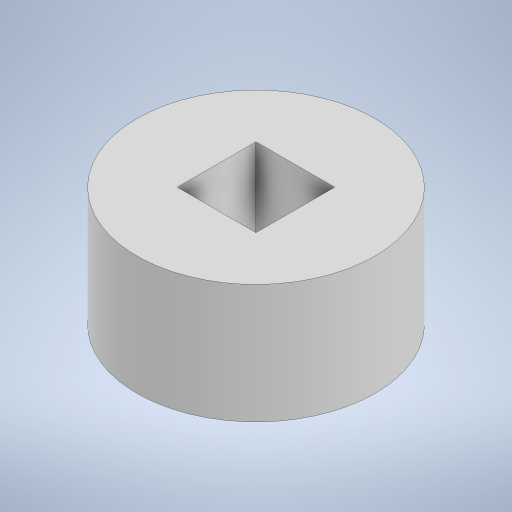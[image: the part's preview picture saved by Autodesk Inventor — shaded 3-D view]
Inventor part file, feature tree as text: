
AUTODESK INVENTOR PART (.ipt)
format: ipt  version: 2023 (Build 270158000, 158)  size: 206,336 bytes
history: native  units: mm
features: extrude x1, sketch x1
ambient origin geometry x8: Origin, YZ Plane, XZ Plane, XY Plane, X Axis, Y Axis, Z Axis, Center Point
bodies: Solid1 (feature_tree)
feature tree (2):
  extrude  "Extrusion1"  Depth=3.302mm
  sketch  "Sketch1"  dims[d0=10.0mm d1=3.302mm d2=3.302mm d3=5.0mm d4=0.0mm]
